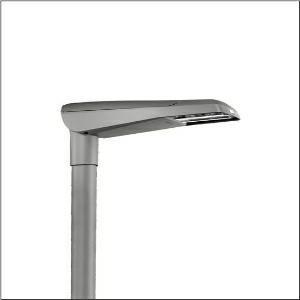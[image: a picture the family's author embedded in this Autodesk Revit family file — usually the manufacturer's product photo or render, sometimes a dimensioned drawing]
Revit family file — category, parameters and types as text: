
# Revit family: streetlight_sl_11_iq_micro___p1_0a_5xc1cc1f08de_50c8
name_source: partatom
category: Lighting Fixtures
units: mm (PartAtom-declared; Revit-internal decimal feet)

## family parameters
Cut with Voids When Loaded = No
Host = Face
Light Source = No
Part Type = Normal
Room Calculation Point = No
Round Connector Dimension = Use Diameter
Shared = No

## types (1)
- --- (1 x LED, 2620 lm, 24.2 W, 2200K)
    Apparent Load = 24 VA
    CIE Flux Codes = 29 63 93 100 100
    Color Rendering = 70
    Color Temperature = 2200K
    Default Elevation = 1800 mm
    Description = Streetlight SL 11 iQ micro, mast luminaire, primary light control with 3 zone facetted reflector, of plastic, silver coated, highly specular, primary optical cover: cover, of PMMA, transparent, light distribution: P1.0a, light emission: direct distribution, primary light characteristic: asymmetric, installation type: post-top, side-entry, lamps: LED, High Power LED, rated values: 3.150lm | 24,1W | 130,7lm/W (begin service life); end service life: 3.150lm | 24,6W; at 50% lumin. flux: 1.575lm | 11,9W | 132,4lm/W, colour temperature: 2200/2700/3000/4000K, colour rendering: CRI > 70, light colour: 722/727/730/740, light setting 1 begin service life: 100% | 3.150lm | 24,1W | 130,7lm/W | 3.000K, light setting 1 end service life: 24,6W, further light settings possible, control: Street-Remote, Auto-Match, Temp-Guard, Lumen-Switch, Night-Set, Smart-Wire, Light-Fading, Desk-Remote (wireless, voltage-free reading and setting of iQ features in the workshop via application-optimized NFC function/RFID function), optimised constant luminous flux control (CLO 2.0), with cable H07RN-F 5x 1.5mm², mains connection: 220..240V, AC, 50/60Hz, connection cable pre-assembled, cable length: 6,5m, luminaire housing, of diecast aluminium, powder-coated, Siteco® metallic grey (DB 702S), please order mast flange separately, inclination adjustable without tools: 0°, 5°, 10°, 15° (post-top) | 0°, -5°, -10°, -15° (side-entry), sealing non-destructively replaceable, multi-level sealing system, length: 600mm, width: 174mm, height: 116mm, mast flange for spigot size: 42mm (side-entry): 5XC10008XM4, 60/48mm (side-entry/post-top): 5XC10108XM2, 76/60mm (side-entry/post-top): 5XC10108XM1, equipment: Power, protection rating (complete): IP66, insulation class (complete): insulation class II (safety insulation), certification: CE, ENEC, ENEC+, VDE, impact resistance: IK10, permissible operating ambient temperature for outdoor applications: -25..+50°C, standard-compliant lighting for roads and squares, Environmental Product Declaration (EPD) tested and certified by an independent institute, packaging unit: 1 piece

Light Distribution: P1.0a
    Height = 116 mm
    Lamp = 1 x LED
    Lamp Light Flux = 2620 lm
    Lamp Power = 24.2 W
    Lamp count = 1
    Length = 600 mm
    Luminous efficacy = 108 lm/W
    Manufacturer = Siteco
    ModVariant = No
    Model = 5XC1CC1F08DE
    Number of Poles = 1
    OnlyDefault = Yes
    Power Factor = 1
    Product Name = Streetlight SL 11 iQ micro | P1.0a
    Product group = mast luminaire | pylon top
    ProductGroupID = 6100
    Protection Class = Protection class II
    Protection Degree = IP 66
    RLX_Detail_Level = 1
    RLX_Emergency_Light_Flux = 0 lm
    RLX_Emergency_Type = 0
    RLX_Emergency_Type_DB = No
    RlxData = <blob elided: 59337 chars, md5=f5eaecba>
    Socket = socket
    Standby Power = 0 W
    System Light Flux = 2620 lm
    System Power = 24 W
    Type Comments = individual setting: luminous flux: 100 % | dim-lin: 254 | 644 mA
    Type Image = l_1006566.jpg
    URL = http://relux.com
    VarID = @adj_037400
    Voltage = 0 V
    Weight = 0.00 kg
    Width = 174 mm

## geometry (parser evidence)
native form markers: Blend x4, Sweep x12
no freeform markers — native parametric forms only
